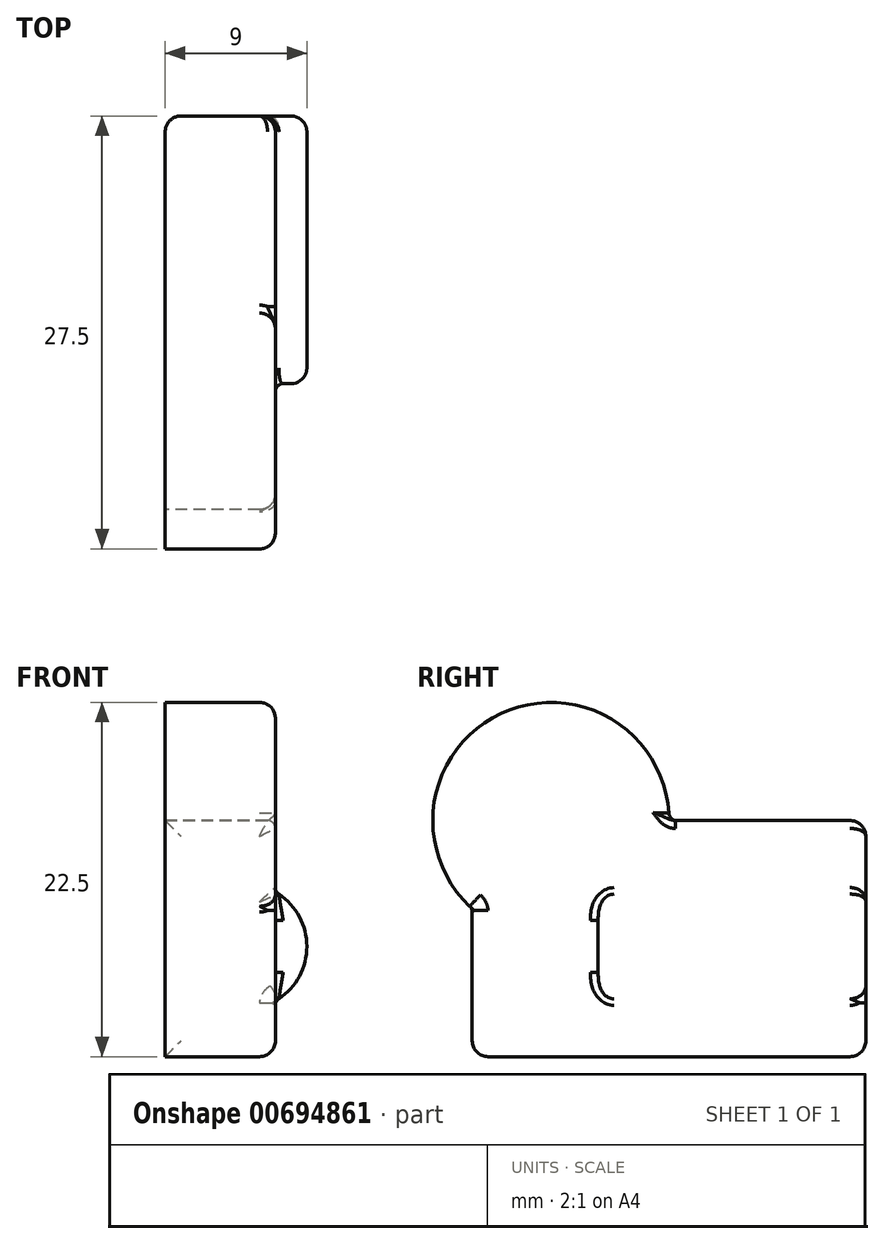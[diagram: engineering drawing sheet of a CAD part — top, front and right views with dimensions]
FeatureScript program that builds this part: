
annotation { "Feature Type Name" : "Feature", "Feature Type Description" : "" }
export const myFeature = defineFeature(function(context is Context, id is Id, definition is map)
    precondition{}
    {
        {
            var Q0;
            Q0=qCreatedBy(makeId("Right.planeOp"),FACE);
            var sketch = newSketch(context, id + "F0", { "sketchPlane" : qUnion([Q0])});
            skCircle(sketch, "E0", {"center": v(0, 0) * mm, "radius": 7.5 * mm});
            skLineSegment(sketch, "E1.bottom", {"start": v(20, -15) * mm, "end": v(-5, -15) * mm});
            skLineSegment(sketch, "E1.top", {"start": v(20, 0) * mm, "end": v(-5, 0) * mm});
            skLineSegment(sketch, "E1.left", {"start": v(20, -15) * mm, "end": v(20, 0) * mm});
            skLineSegment(sketch, "E1.right", {"start": v(-5, -15) * mm, "end": v(-5, 0) * mm});
            skSolve(sketch);
        }
        {
            var Q0;
            {var subQ4=sQuery(id+"F0.wireOp",EDGE,"E1.bottom");Q0=makeQuery(id+"F0.imprint","IMPRINT",FACE,{"disambiguationData":[TD([[makeQuery(id+"F0.imprint","IMPRINT",EDGE,{"derivedFrom":subQ4}),-1.0]])]});}
            var Q1;
            {var subQ0=sQuery(id+"F0.wireOp",EDGE,"E1.top");var subQ1=sQuery(id+"F0.wireOp",EDGE,"E0");var subQ2=makeQuery(id+"F0.imprint","INTERSECT",VERTEX,{"derivedFrom":[subQ1,subQ0]});Q1=makeQuery(id+"F0.imprint","IMPRINT",FACE,{"disambiguationData":[TD([[makeQuery(id+"F0.imprint","IMPRINT",EDGE,{"disambiguationData":[TD([[subQ2,1.0]])],"derivedFrom":subQ1}),1.0]])]});}
            var Q2;
            {var subQ0=sQuery(id+"F0.wireOp",EDGE,"E1.top");var subQ1=sQuery(id+"F0.wireOp",EDGE,"E0");var subQ2=makeQuery(id+"F0.imprint","INTERSECT",VERTEX,{"derivedFrom":[subQ1,subQ0]});Q2=makeQuery(id+"F0.imprint","IMPRINT",FACE,{"disambiguationData":[TD([[makeQuery(id+"F0.imprint","IMPRINT",EDGE,{"disambiguationData":[TD([[subQ2,-1.0]])],"derivedFrom":subQ1}),1.0]])]});}
            extrude(context, id + "F1", {"entities" : qUnion([Q0, Q1, Q2]), "depth" : 7 * mm, "offsetDistance" : 25 * mm});
        }
        {
            var Q0;
            Q0=makeQuery(id+"F1.opExtrude","SWEPT_FACE",FACE,{"disambiguationData":[OSD([sQuery(id+"F0.wireOp",EDGE,"E1.left")])]});
            var sketch = newSketch(context, id + "F2", { "sketchPlane" : qUnion([Q0])});
            skCircle(sketch, "E2", {"center": v(-5, -8) * mm, "radius": 4 * mm});
            skSolve(sketch);
        }
        {
            var Q0;
            {var subQ0=sQuery(id+"F2.wireOp",EDGE,"E2");var subQ1=makeQuery(id+"F1.opExtrude","CAP_EDGE",EDGE,{"disambiguationData":[OSD([sQuery(id+"F0.wireOp",EDGE,"E1.left")])],"isStart":false});var subQ2=makeQuery(id+"F2.imprint","INTERSECT",VERTEX,{"disambiguationData":[OD(0.0)],"derivedFrom":[subQ1,subQ0]});Q0=makeQuery(id+"F2.imprint","IMPRINT",FACE,{"disambiguationData":[TD([[makeQuery(id+"F2.imprint","IMPRINT",EDGE,{"disambiguationData":[TD([[subQ2,1.0]])],"derivedFrom":subQ0}),1.0]])]});}
            var Q1;
            Q1=sQuery(id+"F2.wireOp",EDGE,"E2");
            extrude(context, id + "F3", {"entities" : qUnion([Q0]), "operationType" : NewBodyOperationType.ADD, "surfaceEntities" : qUnion([Q1]), "oppositeDirection" : true, "depth" : 17 * mm, "offsetDistance" : 25 * mm});
        }
        {
            var Q0;
            Q0=makeQuery(id+"F1.opExtrude","SWEPT_EDGE",EDGE,{"disambiguationData":[OSD([sQuery(id+"F0.wireOp",EDGE,"E1.top"),sQuery(id+"F0.wireOp",EDGE,"E1.left")])]});
            var Q1;
            {var subQ0=sQuery(id+"F0.wireOp",EDGE,"E1.left");Q1=makeQuery(id+"F3.boolean.opBoolean","MERGE",FACE,{"derivedFrom":[makeQuery(id+"F1.opExtrude","SWEPT_FACE",FACE,{"disambiguationData":[OSD([subQ0])]}),makeQuery(id+"F3.opExtrude","CAP_FACE",FACE,{"disambiguationData":[OSD([subQ0,sQuery(id+"F2.wireOp",EDGE,"E2")])],"isStart":true})]});}
            var Q2;
            Q2=makeQuery(id+"F1.opExtrude","CAP_EDGE",EDGE,{"disambiguationData":[OSD([sQuery(id+"F0.wireOp",EDGE,"E0")])],"isStart":false});
            var Q3;
            Q3=makeQuery(id+"F1.opExtrude","CAP_EDGE",EDGE,{"disambiguationData":[OSD([sQuery(id+"F0.wireOp",EDGE,"E1.bottom")])],"isStart":false});
            var Q4;
            Q4=makeQuery(id+"F3.opExtrude","CAP_EDGE",EDGE,{"disambiguationData":[OSD([sQuery(id+"F2.wireOp",EDGE,"E2")])],"isStart":false});
            var Q5;
            Q5=makeQuery(id+"F1.opExtrude","CAP_EDGE",EDGE,{"disambiguationData":[OSD([sQuery(id+"F0.wireOp",EDGE,"E1.right")])],"isStart":false});
            var Q6;
            Q6=makeQuery(id+"F1.opExtrude","SWEPT_EDGE",EDGE,{"disambiguationData":[OSD([sQuery(id+"F0.wireOp",EDGE,"E1.bottom"),sQuery(id+"F0.wireOp",EDGE,"E1.right")])]});
            fillet(context, id + "F4", {"entities" : qUnion([Q0, Q1, Q2, Q3, Q4, Q5, Q6]), "radius" : 1 * mm, "tangentPropagation" : true, "allowEdgeOverflow" : false});
        }
        {
            var Q0;
            {var subQ1=sQuery(id+"F0.wireOp",EDGE,"E1.left");var subQ2=sQuery(id+"F0.wireOp",EDGE,"E1.top");Q0=makeQuery(id+"F4.opFillet","BLEND_EDGE",EDGE,{"blendedFrom":[makeQuery(id+"F1.opExtrude","SWEPT_EDGE",EDGE,{"disambiguationData":[OSD([subQ2,subQ1])]}),makeQuery(id+"F3.boolean.opBoolean","SPLIT",EDGE,{"disambiguationData":[TD([makeQuery(id+"F1.opExtrude","SWEPT_FACE",FACE,{"disambiguationData":[OSD([subQ2])]})])],"derivedFrom":makeQuery(id+"F1.opExtrude","CAP_EDGE",EDGE,{"disambiguationData":[OSD([subQ1])],"isStart":false})})],"blendedInto":[]});}
            var Q1;
            Q1=makeQuery(id+"F1.opExtrude","SWEPT_EDGE",EDGE,{"disambiguationData":[OSD([sQuery(id+"F0.wireOp",EDGE,"E0"),sQuery(id+"F0.wireOp",EDGE,"E1.top")])]});
            var Q2;
            {var subQ0=sQuery(id+"F2.wireOp",EDGE,"E2");var subQ1=sQuery(id+"F0.wireOp",EDGE,"E1.left");Q2=makeQuery(id+"F3.opExtrude","SWEPT_EDGE",EDGE,{"disambiguationData":[OSD([subQ1,subQ0]),TDD([makeQuery(id+"F2.imprint","INTERSECT",VERTEX,{"disambiguationData":[OD(0.0)],"derivedFrom":[makeQuery(id+"F1.opExtrude","CAP_EDGE",EDGE,{"disambiguationData":[OSD([subQ1])],"isStart":false}),subQ0]})])]});}
            var Q3;
            Q3=makeQuery(id+"F1.opExtrude","SWEPT_EDGE",EDGE,{"disambiguationData":[OSD([sQuery(id+"F0.wireOp",EDGE,"E0"),sQuery(id+"F0.wireOp",EDGE,"E1.right")])]});
            fillet(context, id + "F5", {"entities" : qUnion([Q0, Q1, Q2, Q3]), "radius" : 0.5 * mm, "tangentPropagation" : true, "allowEdgeOverflow" : false});
        }
    });
